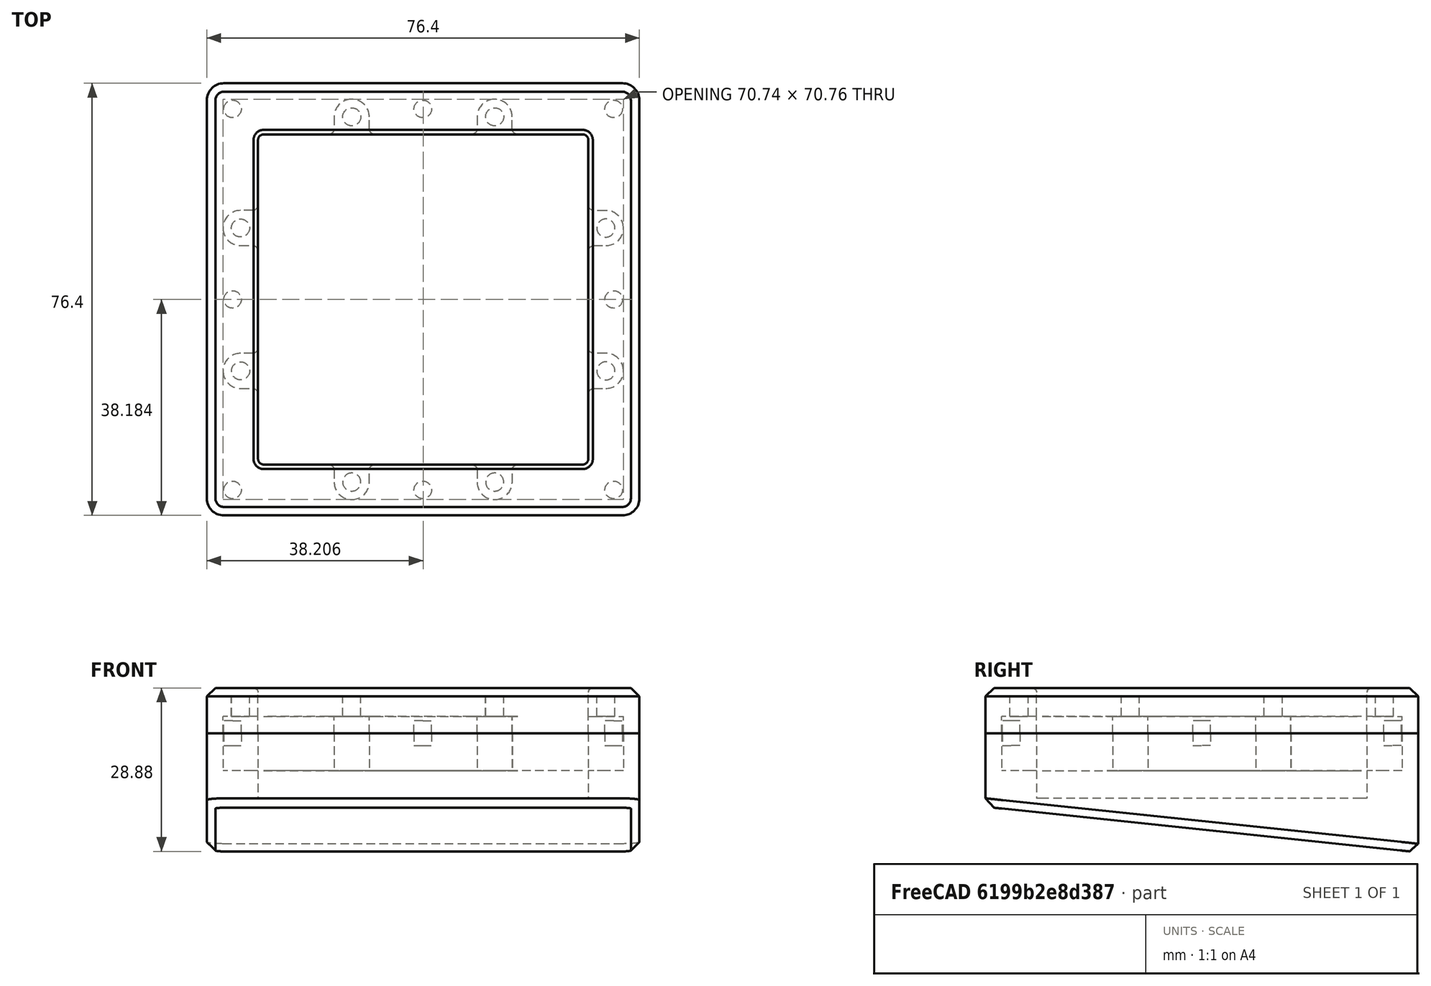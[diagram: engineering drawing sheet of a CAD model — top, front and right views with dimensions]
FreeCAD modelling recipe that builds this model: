
FCSTD DOCUMENT  (FreeCAD 0.21R33771 (Git))
Label: case
License: All rights reserved
LicenseURL: http://en.wikipedia.org/wiki/All_rights_reserved
objects: Part::Feature×28, Part::Cut×8, Part::Extrusion×7, Part::Box×3, Part::MultiFuse×3, Part::Fillet×3, Part::Chamfer×2
note: 54 computed .brp shape members not serialized (recipe doc carries the construction recipe); baked Part::Feature solids carry a one-line shape summary decoded from their .brp

FEATURE [Part::Box] Box  label="立方体"
  AttacherType = Attacher::AttachEngine3D
  Height = 40
  Length = 76.4
  Placement = pos=(0,-76.4,-40) rot=(0,0,1;0rad)
  Width = 76.4
FEATURE [Part::Box] Box001  label="立方体001"
  AttacherType = Attacher::AttachEngine3D
  Height = 40
  Length = 76.4
  Placement = pos=(0,-110,-49.7) rot=(-1,0,0;0.10472rad)
  Width = 150
FEATURE [Part::Box] Box002  label="立方体002"
  AttacherType = Attacher::AttachEngine3D
  Height = 8
  Length = 76.4
  Placement = pos=(0,-76.4,0) rot=(0,0,1;0rad)
  Width = 76.4
FEATURE [Part::Feature] path1951_4_5_5_0_014 .. path1951_4_5_5_0_021  x8 (patterned run collapsed; names and placements below)
  shape: bbox 3.1 x 3.1 x 2e-07 mm, 0 faces, 0 solids (baked)
FEATURE [Part::MultiFuse] Fusion002
  Shapes = -> [path1951_4_5_5_0_021,path1951_4_5_5_0_020,path1951_4_5_5_0_019,path1951_4_5_5_0_018,path1951_4_5_5_0_017,path1951_4_5_5_0_016,path1951_4_5_5_0_015,path1951_4_5_5_0_014]
FEATURE [Part::Extrusion] Extrude002
  Base = -> Fusion002
  Dir = (0,0,1)
  DirMode = 0
  FaceMakerClass = Part::FaceMakerBullseye
  LengthFwd = 2.2
  LengthRev = 0
  Solid = true
  Symmetric = false
FEATURE [Part::Cut] Cut002
  Base = -> Box002
  Tool = -> Extrude002
FEATURE [Part::Feature] path1951_4_5_5_0_5_004
  shape: bbox 70.74 x 70.76 x 2e-07 mm, 0 faces, 0 solids (baked)
FEATURE [Part::Extrusion] Extrude003
  Base = -> path1951_4_5_5_0_5_004
  Dir = (0,0,1)
  DirMode = 0
  FaceMakerClass = Part::FaceMakerBullseye
  LengthFwd = 3
  LengthRev = 0
  Solid = true
  Symmetric = false
FEATURE [Part::Cut] Cut003
  Base = -> Cut002
  Tool = -> Extrude003
FEATURE [Part::Feature] path1951_4_5_5 .. path1951_4_5_012  x8 (patterned run collapsed; names and placements below)
  shape: bbox 3.2 x 3.2 x 2e-07 mm, 0 faces, 0 solids (baked)
FEATURE [Part::MultiFuse] Fusion003
  Placement = pos=(0,0,3) rot=(0,0,1;0rad)
  Shapes = -> [path1951_4_5_012,path1951_4_5_011,path1951_4_5_010,path1951_4_5_009,path1951_4_5_008,path1951_4_5_007,path1951_4_5_006,path1951_4_5_5]
FEATURE [Part::Extrusion] Extrude004
  Base = -> Fusion003
  Dir = (0,0,1)
  DirMode = 0
  FaceMakerClass = Part::FaceMakerBullseye
  LengthFwd = 3.5
  LengthRev = 0
  Solid = true
  Symmetric = false
FEATURE [Part::Cut] Cut004
  Base = -> Cut003
  Tool = -> Extrude004
FEATURE [Part::Feature] path1951_4_5_5_0
  shape: bbox 58.34 x 58.36 x 2e-07 mm, 0 faces, 0 solids (baked)
FEATURE [Part::Extrusion] Extrude005
  Base = -> path1951_4_5_5_0
  Dir = (0,0,1)
  DirMode = 0
  FaceMakerClass = Part::FaceMakerBullseye
  LengthFwd = 8
  LengthRev = 0
  Solid = true
  Symmetric = false
FEATURE [Part::Cut] Cut005
  Base = -> Cut004
  Tool = -> Extrude005
FEATURE [Part::Fillet] Fillet001
  Base = -> Cut005
  Edges = 4 edges r=3: [Edge1,Edge3,Edge6,Edge19]
FEATURE [Part::Chamfer] Chamfer001
  Base = -> Fillet001
  Edges = 1 edges r=1.5: [Edge7]
FEATURE [Part::Fillet] Fillet002  label="top"
  Base = -> Chamfer001
  Edges = 1 edges r=0.8: [Edge127]
FEATURE [Part::Cut] Cut
  Base = -> Box
  Tool = -> Box001
FEATURE [Part::Feature] path1951_4_5_5_0_5_3
  shape: bbox 70.74 x 70.76 x 2e-07 mm, 0 faces, 0 solids (baked)
FEATURE [Part::Extrusion] Extrude
  Base = -> path1951_4_5_5_0_5_3
  Dir = (0,0,-1)
  DirMode = 0
  FaceMakerClass = Part::FaceMakerBullseye
  LengthFwd = 6.6
  LengthRev = 0
  Solid = true
  Symmetric = false
FEATURE [Part::Cut] Cut006
  Base = -> Cut
  Tool = -> Extrude
FEATURE [Part::Feature] path1951_4_5_5_001
  Placement = pos=(0,0,-6.6) rot=(0,0,1;0rad)
  shape: bbox 58.34 x 58.36 x 2e-07 mm, 0 faces, 0 solids (baked)
FEATURE [Part::Extrusion] Extrude006
  Base = -> path1951_4_5_5_001
  Dir = (0,0,-1)
  DirMode = 0
  FaceMakerClass = Part::FaceMakerBullseye
  LengthFwd = 4.9
  LengthRev = 0
  Solid = true
  Symmetric = false
FEATURE [Part::Cut] Cut007
  Base = -> Cut006
  Tool = -> Extrude006
FEATURE [Part::Feature] path1951_4_5_5_0_5
  shape: bbox 3.1 x 3.1 x 2e-07 mm, 0 faces, 0 solids (baked)
FEATURE [Part::Feature] path1951_4_5_5_0_022 .. path1951_4_5_5_0_028  x7 (patterned run collapsed; names and placements below)
  shape: bbox 3.1 x 3.1 x 2e-07 mm, 0 faces, 0 solids (baked)
FEATURE [Part::MultiFuse] Fusion
  Shapes = -> [path1951_4_5_5_0_028,path1951_4_5_5_0_026,path1951_4_5_5_0_027,path1951_4_5_5_0_025,path1951_4_5_5_0_024,path1951_4_5_5_0_023,path1951_4_5_5_0_022,path1951_4_5_5_0_5]
FEATURE [Part::Extrusion] Extrude007
  Base = -> Fusion
  Dir = (0,0,-1)
  DirMode = 0
  FaceMakerClass = Part::FaceMakerBullseye
  LengthFwd = 2.2
  LengthRev = 0
  Solid = true
  Symmetric = false
FEATURE [Part::Cut] Cut008
  Base = -> Cut007
  Tool = -> Extrude007
FEATURE [Part::Fillet] Fillet
  Base = -> Cut008
  Edges = 4 edges r=3: [Edge1,Edge3,Edge5,Edge106]
FEATURE [Part::Chamfer] Chamfer  label="bottom"
  Base = -> Fillet
  Edges = 1 edges r=1.5: [Edge112]
